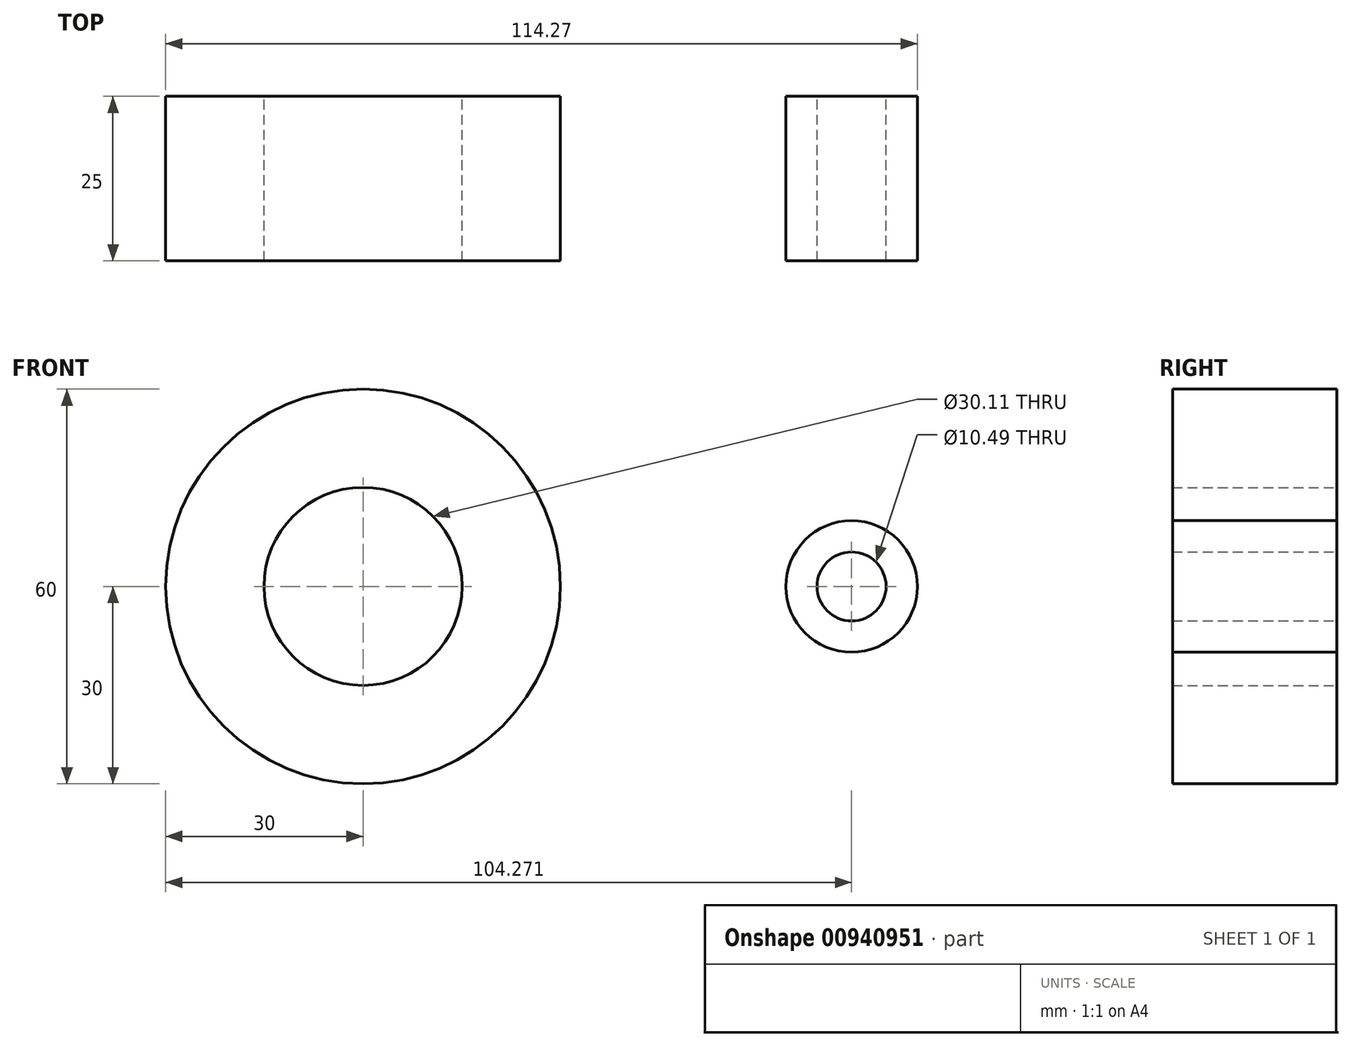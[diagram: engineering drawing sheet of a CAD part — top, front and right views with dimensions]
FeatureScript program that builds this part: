
annotation { "Feature Type Name" : "Feature", "Feature Type Description" : "" }
export const myFeature = defineFeature(function(context is Context, id is Id, definition is map)
    precondition{}
    {
        {
            var Q0;
            Q0=qCreatedBy(makeId("Front.planeOp"),FACE);
            var sketch = newSketch(context, id + "F0", { "sketchPlane" : qUnion([Q0])});
            skCircle(sketch, "E0", {"center": v(0, 0) * mm, "radius": 30 * mm});
            skCircle(sketch, "E1", {"center": v(74.27, 0) * mm, "radius": 10 * mm});
            skLineSegment(sketch, "E2", {"start": v(9.44, 28.48) * mm, "end": v(76.96, 9.63) * mm});
            skLineSegment(sketch, "E3", {"start": v(6.12, -29.37) * mm, "end": v(73.78, -10.52) * mm});
            skCircle(sketch, "E4", {"center": v(0, 0) * mm, "radius": 15.05 * mm});
            skCircle(sketch, "E5", {"center": v(74.27, 0) * mm, "radius": 5.24 * mm});
            skSolve(sketch);
        }
        {
            var Q0;
            Q0 = qSketchRegion(id + "F0", true);
            extrude(context, id + "F1", {"entities" : qUnion([Q0]), "depth" : 25 * mm, "offsetDistance" : 25 * mm});
        }
    });
